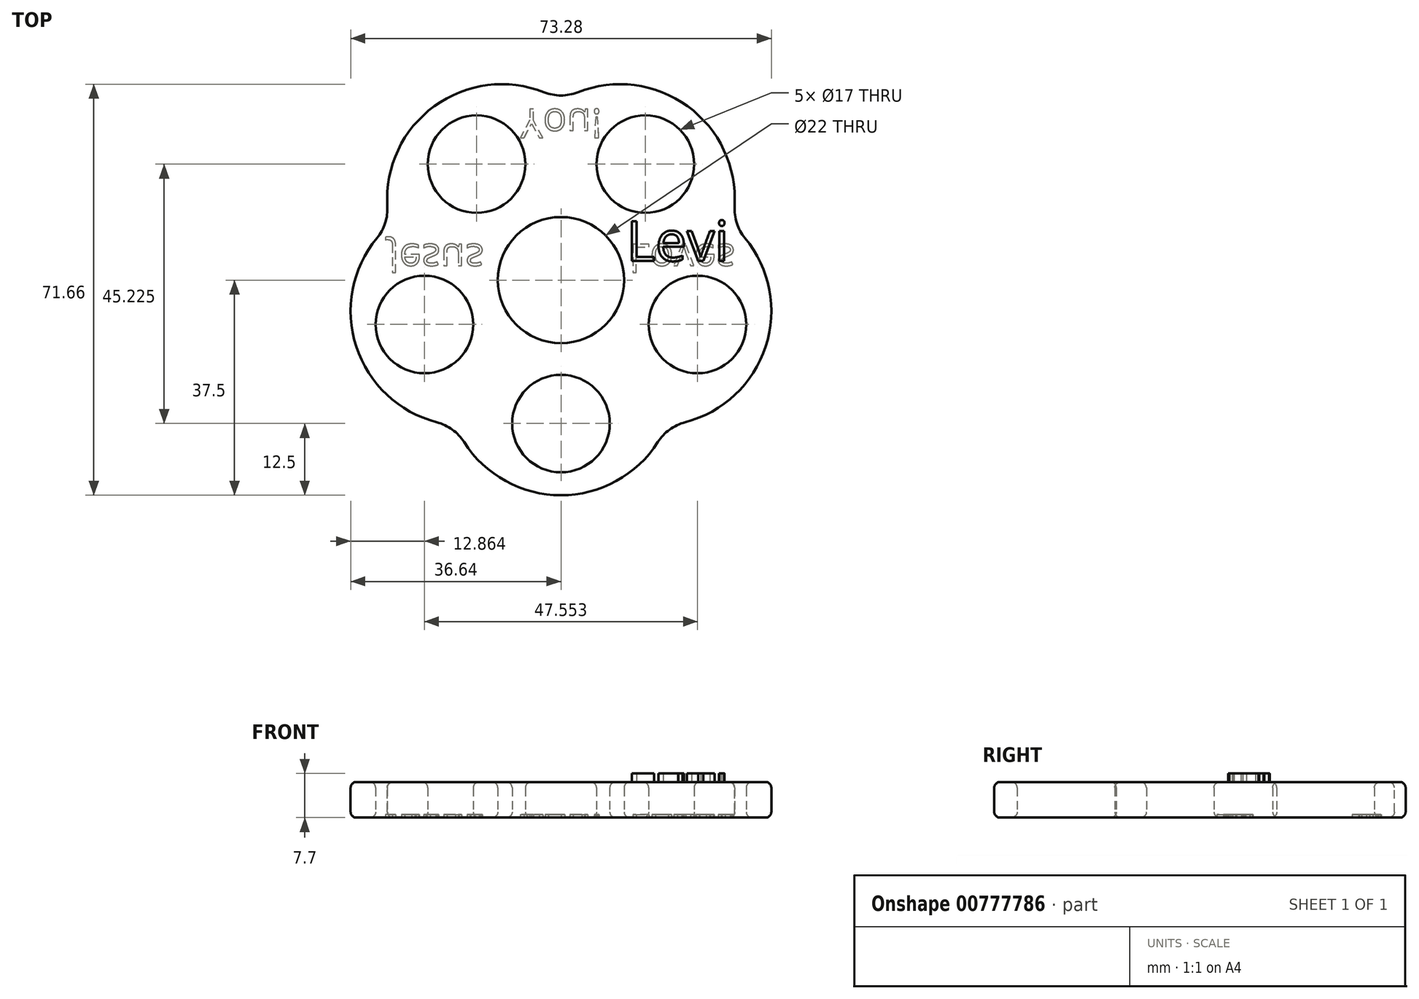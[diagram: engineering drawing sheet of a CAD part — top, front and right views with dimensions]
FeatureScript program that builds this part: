
annotation { "Feature Type Name" : "Feature", "Feature Type Description" : "" }
export const myFeature = defineFeature(function(context is Context, id is Id, definition is map)
    precondition{}
    {
        {
            var Q0;
            Q0=qCreatedBy(makeId("Top.planeOp"),FACE);
            var sketch = newSketch(context, id + "F0", { "sketchPlane" : qUnion([Q0])});
            skCircle(sketch, "E0.cCircle", {"center": v(0, 0) * mm, "radius": 17.5 * mm, "construction": true});
            skPoint(sketch, "E0.0.midPoint", {"position": v(10.29, 14.16) * mm});
            skArc(sketch, "E1", {"start": v(0, 31.3) * mm, "mid": v(-22.04, 30.34) * mm, "end": v(-29.78, 9.68) * mm});
            skArc(sketch, "E2", {"start": v(29.78, 9.68) * mm, "mid": v(22.04, 30.34) * mm, "end": v(0, 31.3) * mm});
            skArc(sketch, "E3", {"start": v(18.4, -25.33) * mm, "mid": v(35.66, -11.59) * mm, "end": v(29.78, 9.68) * mm});
            skArc(sketch, "E4", {"start": v(-18.4, -25.33) * mm, "mid": v(0, -37.5) * mm, "end": v(18.4, -25.33) * mm});
            skArc(sketch, "E5", {"start": v(-29.78, 9.68) * mm, "mid": v(-35.66, -11.59) * mm, "end": v(-18.4, -25.33) * mm});
            skCircle(sketch, "E6", {"center": v(0, 0) * mm, "radius": 31.3 * mm, "construction": true});
            skCircle(sketch, "E7", {"center": v(0, 0) * mm, "radius": 11 * mm});
            skCircle(sketch, "E8", {"center": v(-14.7, 20.23) * mm, "radius": 8.5 * mm});
            skCircle(sketch, "E9", {"center": v(14.7, 20.23) * mm, "radius": 8.5 * mm});
            skCircle(sketch, "E10", {"center": v(23.78, -7.73) * mm, "radius": 8.5 * mm});
            skCircle(sketch, "E11", {"center": v(0, -25) * mm, "radius": 8.5 * mm});
            skCircle(sketch, "E12", {"center": v(-23.78, -7.73) * mm, "radius": 8.5 * mm});
            skCircle(sketch, "E13", {"center": v(0, 0) * mm, "radius": 25 * mm, "construction": true});
            skLineSegment(sketch, "E14", {"start": v(0, 0) * mm, "end": v(0, 61.86) * mm, "construction": true});
            skLineSegment(sketch, "E15", {"start": v(0, 0) * mm, "end": v(34.06, 46.88) * mm, "construction": true});
            skLineSegment(sketch, "E16", {"start": v(0, 0) * mm, "end": v(68.87, -22.38) * mm, "construction": true});
            skLineSegment(sketch, "E17", {"start": v(0, 0) * mm, "end": v(0, -33.5) * mm, "construction": true});
            skLineSegment(sketch, "E18", {"start": v(0, 0) * mm, "end": v(-60.43, -19.63) * mm, "construction": true});
            skLineSegment(sketch, "E19", {"start": v(0, 0) * mm, "end": v(-30.72, 42.28) * mm, "construction": true});
            skSolve(sketch);
        }
        {
            var Q0;
            Q0=qSketchRegion(id+"F0",true);
            extrude(context, id + "F1", {"entities" : qUnion([Q0]), "depth" : 6.2 * mm, "offsetDistance" : 25.4 * mm});
        }
        {
            var Q0;
            Q0=makeQuery(id+"F1.opExtrude","SWEPT_EDGE",EDGE,{"disambiguationData":[OSD([sQuery(id+"F0.wireOp",EDGE,"E3"),sQuery(id+"F0.wireOp",EDGE,"E4")])]});
            var Q1;
            Q1=makeQuery(id+"F1.opExtrude","SWEPT_EDGE",EDGE,{"disambiguationData":[OSD([sQuery(id+"F0.wireOp",EDGE,"E2"),sQuery(id+"F0.wireOp",EDGE,"E3")])]});
            var Q2;
            Q2=makeQuery(id+"F1.opExtrude","SWEPT_EDGE",EDGE,{"disambiguationData":[OSD([sQuery(id+"F0.wireOp",EDGE,"E1"),sQuery(id+"F0.wireOp",EDGE,"E2")])]});
            var Q3;
            Q3=makeQuery(id+"F1.opExtrude","SWEPT_EDGE",EDGE,{"disambiguationData":[OSD([sQuery(id+"F0.wireOp",EDGE,"E1"),sQuery(id+"F0.wireOp",EDGE,"E5")])]});
            var Q4;
            Q4=makeQuery(id+"F1.opExtrude","SWEPT_EDGE",EDGE,{"disambiguationData":[OSD([sQuery(id+"F0.wireOp",EDGE,"E4"),sQuery(id+"F0.wireOp",EDGE,"E5")])]});
            fillet(context, id + "F2", {"entities" : qUnion([Q0, Q1, Q2, Q3, Q4]), "radius" : 8 * mm, "tangentPropagation" : true, "allowEdgeOverflow" : false});
        }
        {
            var Q0;
            Q0=makeQuery(id+"F1.opExtrude","CAP_FACE",FACE,{"disambiguationData":[OSD([sQuery(id+"F0.wireOp",EDGE,"E1"),sQuery(id+"F0.wireOp",EDGE,"E2"),sQuery(id+"F0.wireOp",EDGE,"E3"),sQuery(id+"F0.wireOp",EDGE,"E4"),sQuery(id+"F0.wireOp",EDGE,"E5"),sQuery(id+"F0.wireOp",EDGE,"E7"),sQuery(id+"F0.wireOp",EDGE,"E8"),sQuery(id+"F0.wireOp",EDGE,"E9"),sQuery(id+"F0.wireOp",EDGE,"E10"),sQuery(id+"F0.wireOp",EDGE,"E11"),sQuery(id+"F0.wireOp",EDGE,"E12")])],"isStart":false});
            var Q1;
            Q1=makeQuery(id+"F1.opExtrude","CAP_FACE",FACE,{"disambiguationData":[OSD([sQuery(id+"F0.wireOp",EDGE,"E1"),sQuery(id+"F0.wireOp",EDGE,"E2"),sQuery(id+"F0.wireOp",EDGE,"E3"),sQuery(id+"F0.wireOp",EDGE,"E4"),sQuery(id+"F0.wireOp",EDGE,"E5"),sQuery(id+"F0.wireOp",EDGE,"E7"),sQuery(id+"F0.wireOp",EDGE,"E8"),sQuery(id+"F0.wireOp",EDGE,"E9"),sQuery(id+"F0.wireOp",EDGE,"E10"),sQuery(id+"F0.wireOp",EDGE,"E11"),sQuery(id+"F0.wireOp",EDGE,"E12")])],"isStart":true});
            fillet(context, id + "F3", {"entities" : qUnion([Q0, Q1]), "radius" : 1 * mm, "tangentPropagation" : true, "allowEdgeOverflow" : false});
        }
        {
            var Q0;
            Q0=makeQuery(id+"F1.opExtrude","CAP_FACE",FACE,{"disambiguationData":[OSD([sQuery(id+"F0.wireOp",EDGE,"E1"),sQuery(id+"F0.wireOp",EDGE,"E2"),sQuery(id+"F0.wireOp",EDGE,"E3"),sQuery(id+"F0.wireOp",EDGE,"E4"),sQuery(id+"F0.wireOp",EDGE,"E5"),sQuery(id+"F0.wireOp",EDGE,"E7"),sQuery(id+"F0.wireOp",EDGE,"E8"),sQuery(id+"F0.wireOp",EDGE,"E9"),sQuery(id+"F0.wireOp",EDGE,"E10"),sQuery(id+"F0.wireOp",EDGE,"E11"),sQuery(id+"F0.wireOp",EDGE,"E12")])],"isStart":false});
            var sketch = newSketch(context, id + "F4", { "sketchPlane" : qUnion([Q0])});
            skText(sketch, "E20", { "text": "Levi", "fontName": "OpenSans-Regular.ttf"});
            const initialGuessF4  = {"E20": [0.01141, 0.00335, 1, 0, 0.007]};
            skSetInitialGuess(sketch, initialGuessF4);
            skSolve(sketch);
        }
        {
            var Q0;
            Q0=qSketchRegion(id+"F4",true);
            extrude(context, id + "F5", {"entities" : qUnion([Q0]), "operationType" : NewBodyOperationType.ADD, "depth" : 1.5 * mm, "offsetDistance" : 25 * mm});
        }
        {
            var Q0;
            Q0=makeQuery(id+"F1.opExtrude","CAP_FACE",FACE,{"disambiguationData":[OSD([sQuery(id+"F0.wireOp",EDGE,"E1"),sQuery(id+"F0.wireOp",EDGE,"E2"),sQuery(id+"F0.wireOp",EDGE,"E3"),sQuery(id+"F0.wireOp",EDGE,"E4"),sQuery(id+"F0.wireOp",EDGE,"E5"),sQuery(id+"F0.wireOp",EDGE,"E7"),sQuery(id+"F0.wireOp",EDGE,"E8"),sQuery(id+"F0.wireOp",EDGE,"E9"),sQuery(id+"F0.wireOp",EDGE,"E10"),sQuery(id+"F0.wireOp",EDGE,"E11"),sQuery(id+"F0.wireOp",EDGE,"E12")])],"isStart":true});
            var sketch = newSketch(context, id + "F6", { "sketchPlane" : qUnion([Q0])});
            skText(sketch, "E21", { "text": "Jesus              Loves", "fontName": "OpenSans-Regular.ttf"});
            skText(sketch, "E22", { "text": "You!", "fontName": "OpenSans-Regular.ttf"});
            const initialGuessF6  = {"E21": [-0.03003, -0.00626, 1, 0, 0.005], "E22": [-0.00706, -0.0298, 1, 0, 0.005]};
            skSetInitialGuess(sketch, initialGuessF6);
            skSolve(sketch);
        }
        {
            var Q0;
            Q0=qSketchRegion(id+"F6",true);
            extrude(context, id + "F7", {"entities" : qUnion([Q0]), "operationType" : NewBodyOperationType.REMOVE, "oppositeDirection" : true, "depth" : .5 * mm, "offsetDistance" : 25 * mm});
        }
    });
